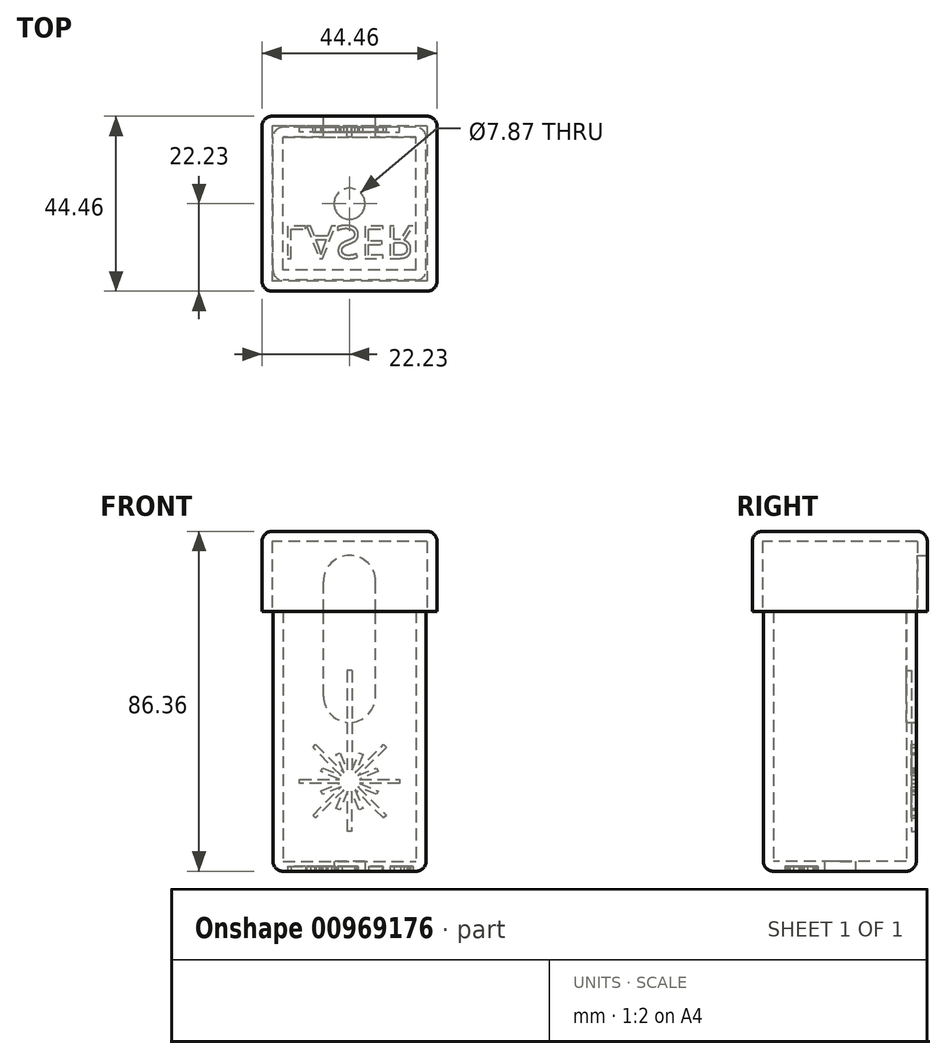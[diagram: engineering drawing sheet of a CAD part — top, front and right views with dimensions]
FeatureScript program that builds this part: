
annotation { "Feature Type Name" : "Feature", "Feature Type Description" : "" }
export const myFeature = defineFeature(function(context is Context, id is Id, definition is map)
    precondition{}
    {
        {
            var Q0;
            Q0=qCreatedBy(makeId("Top.planeOp"),FACE);
            var sketch = newSketch(context, id + "F0", { "sketchPlane" : qUnion([Q0])});
            skLineSegment(sketch, "E0.bottom", {"start": v(16.9, -16.9) * mm, "end": v(-16.9, -16.9) * mm});
            skLineSegment(sketch, "E0.top", {"start": v(16.9, 16.9) * mm, "end": v(-16.9, 16.9) * mm});
            skLineSegment(sketch, "E0.left", {"start": v(16.9, -16.9) * mm, "end": v(16.9, 16.9) * mm});
            skLineSegment(sketch, "E0.right", {"start": v(-16.9, -16.9) * mm, "end": v(-16.9, 16.9) * mm});
            skPoint(sketch, "E0.middle", {"position": v(0, 0) * mm});
            skLineSegment(sketch, "E1.bottom", {"start": v(19.43, -19.43) * mm, "end": v(-19.43, -19.43) * mm});
            skLineSegment(sketch, "E1.top", {"start": v(19.43, 19.43) * mm, "end": v(-19.43, 19.43) * mm});
            skLineSegment(sketch, "E1.left", {"start": v(19.43, -19.43) * mm, "end": v(19.43, 19.43) * mm});
            skLineSegment(sketch, "E1.right", {"start": v(-19.43, -19.43) * mm, "end": v(-19.43, 19.43) * mm});
            skSolve(sketch);
        }
        {
            var Q0;
            Q0=makeQuery(id+"F0.imprint","IMPRINT",FACE,{"disambiguationData":[TD([[makeQuery(id+"F0.imprint","IMPRINT",EDGE,{"derivedFrom":sQuery(id+"F0.wireOp",EDGE,"E0.bottom")}),1.0]])]});
            var Q1;
            Q1=makeQuery(id+"F0.imprint","IMPRINT",FACE,{"disambiguationData":[TD([[makeQuery(id+"F0.imprint","IMPRINT",EDGE,{"derivedFrom":sQuery(id+"F0.wireOp",EDGE,"E0.bottom")}),-1.0]])]});
            extrude(context, id + "F1", {"entities" : qUnion([Q0, Q1]), "depth" : 2.54 * mm, "offsetDistance" : 25.4 * mm});
        }
        {
            var Q0;
            Q0 = qSketchRegion(id + "F0", true);
            extrude(context, id + "F2", {"entities" : qUnion([Q0]), "operationType" : NewBodyOperationType.ADD, "depth" : 66.04 * mm, "offsetDistance" : 25.4 * mm});
        }
        {
            var Q0;
            {var subQ0=sQuery(id+"F0.wireOp",EDGE,"E1.left");var subQ1=sQuery(id+"F0.wireOp",EDGE,"E1.bottom");Q0=makeQuery(id+"F2.boolean.opBoolean","MERGE",EDGE,{"derivedFrom":[makeQuery(id+"F1.opExtrude","SWEPT_EDGE",EDGE,{"disambiguationData":[OSD([subQ1,subQ0])]}),makeQuery(id+"F2.opExtrude","SWEPT_EDGE",EDGE,{"disambiguationData":[OSD([subQ1,subQ0])]})]});}
            var Q1;
            {var subQ0=sQuery(id+"F0.wireOp",EDGE,"E1.left");var subQ1=sQuery(id+"F0.wireOp",EDGE,"E1.top");Q1=makeQuery(id+"F2.boolean.opBoolean","MERGE",EDGE,{"derivedFrom":[makeQuery(id+"F1.opExtrude","SWEPT_EDGE",EDGE,{"disambiguationData":[OSD([subQ1,subQ0])]}),makeQuery(id+"F2.opExtrude","SWEPT_EDGE",EDGE,{"disambiguationData":[OSD([subQ1,subQ0])]})]});}
            var Q2;
            Q2=makeQuery(id+"F1.opExtrude","CAP_EDGE",EDGE,{"disambiguationData":[OSD([sQuery(id+"F0.wireOp",EDGE,"E1.left")])],"isStart":true});
            var Q3;
            Q3=makeQuery(id+"F1.opExtrude","CAP_EDGE",EDGE,{"disambiguationData":[OSD([sQuery(id+"F0.wireOp",EDGE,"E1.bottom")])],"isStart":true});
            var Q4;
            {var subQ0=sQuery(id+"F0.wireOp",EDGE,"E1.right");var subQ1=sQuery(id+"F0.wireOp",EDGE,"E1.bottom");Q4=makeQuery(id+"F2.boolean.opBoolean","MERGE",EDGE,{"derivedFrom":[makeQuery(id+"F1.opExtrude","SWEPT_EDGE",EDGE,{"disambiguationData":[OSD([subQ1,subQ0])]}),makeQuery(id+"F2.opExtrude","SWEPT_EDGE",EDGE,{"disambiguationData":[OSD([subQ1,subQ0])]})]});}
            var Q5;
            Q5=makeQuery(id+"F1.opExtrude","CAP_EDGE",EDGE,{"disambiguationData":[OSD([sQuery(id+"F0.wireOp",EDGE,"E1.right")])],"isStart":true});
            var Q6;
            Q6=makeQuery(id+"F1.opExtrude","CAP_EDGE",EDGE,{"disambiguationData":[OSD([sQuery(id+"F0.wireOp",EDGE,"E1.top")])],"isStart":true});
            var Q7;
            {var subQ0=sQuery(id+"F0.wireOp",EDGE,"E1.right");var subQ1=sQuery(id+"F0.wireOp",EDGE,"E1.top");Q7=makeQuery(id+"F2.boolean.opBoolean","MERGE",EDGE,{"derivedFrom":[makeQuery(id+"F1.opExtrude","SWEPT_EDGE",EDGE,{"disambiguationData":[OSD([subQ1,subQ0])]}),makeQuery(id+"F2.opExtrude","SWEPT_EDGE",EDGE,{"disambiguationData":[OSD([subQ1,subQ0])]})]});}
            fillet(context, id + "F3", {"entities" : qUnion([Q0, Q1, Q2, Q3, Q4, Q5, Q6, Q7]), "radius" : 2.54 * mm, "tangentPropagation" : true, "allowEdgeOverflow" : false});
        }
        {
            var Q0;
            Q0=makeQuery(id+"F1.opExtrude","CAP_FACE",FACE,{"disambiguationData":[OSD([sQuery(id+"F0.wireOp",EDGE,"E1.bottom"),sQuery(id+"F0.wireOp",EDGE,"E1.top"),sQuery(id+"F0.wireOp",EDGE,"E1.left"),sQuery(id+"F0.wireOp",EDGE,"E1.right")])],"isStart":true});
            var sketch = newSketch(context, id + "F4", { "sketchPlane" : qUnion([Q0])});
            skCircle(sketch, "E2", {"center": v(0, 0) * mm, "radius": 3.94 * mm});
            skSolve(sketch);
        }
        {
            var Q0;
            Q0=makeQuery(id+"F4.imprint","IMPRINT",FACE,{"disambiguationData":[TD([[makeQuery(id+"F4.imprint","IMPRINT",EDGE,{"derivedFrom":sQuery(id+"F4.wireOp",EDGE,"E2")}),1.0]])]});
            extrude(context, id + "F5", {"entities" : qUnion([Q0]), "operationType" : NewBodyOperationType.REMOVE, "oppositeDirection" : true, "depth" : 25.4 * mm, "offsetDistance" : 25.4 * mm});
        }
        {
            var Q0;
            Q0=makeQuery(id+"F2.opExtrude","CAP_FACE",FACE,{"disambiguationData":[OSD([sQuery(id+"F0.wireOp",EDGE,"E0.bottom"),sQuery(id+"F0.wireOp",EDGE,"E0.top"),sQuery(id+"F0.wireOp",EDGE,"E0.left"),sQuery(id+"F0.wireOp",EDGE,"E0.right"),sQuery(id+"F0.wireOp",EDGE,"E1.bottom"),sQuery(id+"F0.wireOp",EDGE,"E1.top"),sQuery(id+"F0.wireOp",EDGE,"E1.left"),sQuery(id+"F0.wireOp",EDGE,"E1.right")])],"isStart":false});
            var sketch = newSketch(context, id + "F6", { "sketchPlane" : qUnion([Q0])});
            skLineSegment(sketch, "E3.bottom", {"start": v(19.69, 19.69) * mm, "end": v(-19.69, 19.69) * mm});
            skLineSegment(sketch, "E3.top", {"start": v(19.69, -19.69) * mm, "end": v(-19.69, -19.69) * mm});
            skLineSegment(sketch, "E3.left", {"start": v(19.69, 19.69) * mm, "end": v(19.69, -19.69) * mm});
            skLineSegment(sketch, "E3.right", {"start": v(-19.69, 19.69) * mm, "end": v(-19.69, -19.69) * mm});
            skPoint(sketch, "E3.middle", {"position": v(0, 0) * mm});
            skLineSegment(sketch, "E4.bottom", {"start": v(22.23, 22.23) * mm, "end": v(-22.23, 22.23) * mm});
            skLineSegment(sketch, "E4.top", {"start": v(22.23, -22.23) * mm, "end": v(-22.23, -22.23) * mm});
            skLineSegment(sketch, "E4.left", {"start": v(22.23, 22.23) * mm, "end": v(22.23, -22.23) * mm});
            skLineSegment(sketch, "E4.right", {"start": v(-22.23, 22.23) * mm, "end": v(-22.23, -22.23) * mm});
            skSolve(sketch);
        }
        {
            var Q0;
            Q0=makeQuery(id+"F6.imprint","IMPRINT",FACE,{"disambiguationData":[TD([[makeQuery(id+"F6.imprint","IMPRINT",EDGE,{"derivedFrom":sQuery(id+"F6.wireOp",EDGE,"E3.bottom")}),-1.0]])]});
            extrude(context, id + "F7", {"entities" : qUnion([Q0]), "depth" : 17.78 * mm, "offsetDistance" : 25.4 * mm});
        }
        {
            var Q0;
            Q0=makeQuery(id+"F7.opExtrude","CAP_FACE",FACE,{"disambiguationData":[OSD([sQuery(id+"F6.wireOp",EDGE,"E3.bottom"),sQuery(id+"F6.wireOp",EDGE,"E3.top"),sQuery(id+"F6.wireOp",EDGE,"E3.left"),sQuery(id+"F6.wireOp",EDGE,"E3.right"),sQuery(id+"F6.wireOp",EDGE,"E4.bottom"),sQuery(id+"F6.wireOp",EDGE,"E4.top"),sQuery(id+"F6.wireOp",EDGE,"E4.left"),sQuery(id+"F6.wireOp",EDGE,"E4.right")])],"isStart":false});
            var sketch = newSketch(context, id + "F8", { "sketchPlane" : qUnion([Q0])});
            skLineSegment(sketch, "E5.bottom", {"start": v(19.69, 19.69) * mm, "end": v(-19.69, 19.69) * mm});
            skLineSegment(sketch, "E5.top", {"start": v(19.69, -19.69) * mm, "end": v(-19.69, -19.69) * mm});
            skLineSegment(sketch, "E5.left", {"start": v(19.69, 19.69) * mm, "end": v(19.69, -19.69) * mm});
            skLineSegment(sketch, "E5.right", {"start": v(-19.69, 19.69) * mm, "end": v(-19.69, -19.69) * mm});
            skPoint(sketch, "E5.middle", {"position": v(0, 0) * mm});
            skLineSegment(sketch, "E6.bottom", {"start": v(22.22, 22.23) * mm, "end": v(-22.23, 22.23) * mm});
            skLineSegment(sketch, "E6.top", {"start": v(22.22, -22.23) * mm, "end": v(-22.23, -22.23) * mm});
            skLineSegment(sketch, "E6.left", {"start": v(22.22, 22.23) * mm, "end": v(22.22, -22.23) * mm});
            skLineSegment(sketch, "E6.right", {"start": v(-22.23, 22.23) * mm, "end": v(-22.23, -22.23) * mm});
            skSolve(sketch);
        }
        {
            var Q0;
            Q0=makeQuery(id+"F8.imprint","IMPRINT",FACE,{"disambiguationData":[TD([[makeQuery(id+"F8.imprint","IMPRINT",EDGE,{"derivedFrom":sQuery(id+"F8.wireOp",EDGE,"E5.bottom")}),1.0]])]});
            var Q1;
            Q1=makeQuery(id+"F8.imprint","IMPRINT",FACE,{"disambiguationData":[TD([[makeQuery(id+"F8.imprint","IMPRINT",EDGE,{"derivedFrom":sQuery(id+"F8.wireOp",EDGE,"E5.bottom")}),-1.0]])]});
            extrude(context, id + "F9", {"entities" : qUnion([Q0, Q1]), "operationType" : NewBodyOperationType.ADD, "depth" : 2.54 * mm, "offsetDistance" : 25.4 * mm});
        }
        {
            var Q0;
            Q0=makeQuery(id+"F9.boolean.opBoolean","MERGE",EDGE,{"derivedFrom":[makeQuery(id+"F7.opExtrude","SWEPT_EDGE",EDGE,{"disambiguationData":[OSD([sQuery(id+"F6.wireOp",EDGE,"E4.top"),sQuery(id+"F6.wireOp",EDGE,"E4.left")])]}),makeQuery(id+"F9.opExtrude","SWEPT_EDGE",EDGE,{"disambiguationData":[OSD([sQuery(id+"F8.wireOp",EDGE,"E6.top"),sQuery(id+"F8.wireOp",EDGE,"E6.left")])]})]});
            var Q1;
            Q1=makeQuery(id+"F9.opExtrude","CAP_EDGE",EDGE,{"disambiguationData":[OSD([sQuery(id+"F8.wireOp",EDGE,"E6.left")])],"isStart":false});
            var Q2;
            Q2=makeQuery(id+"F9.opExtrude","CAP_EDGE",EDGE,{"disambiguationData":[OSD([sQuery(id+"F8.wireOp",EDGE,"E6.top")])],"isStart":false});
            var Q3;
            Q3=makeQuery(id+"F9.boolean.opBoolean","MERGE",EDGE,{"derivedFrom":[makeQuery(id+"F7.opExtrude","SWEPT_EDGE",EDGE,{"disambiguationData":[OSD([sQuery(id+"F6.wireOp",EDGE,"E4.bottom"),sQuery(id+"F6.wireOp",EDGE,"E4.left")])]}),makeQuery(id+"F9.opExtrude","SWEPT_EDGE",EDGE,{"disambiguationData":[OSD([sQuery(id+"F8.wireOp",EDGE,"E6.bottom"),sQuery(id+"F8.wireOp",EDGE,"E6.left")])]})]});
            var Q4;
            Q4=makeQuery(id+"F9.opExtrude","CAP_EDGE",EDGE,{"disambiguationData":[OSD([sQuery(id+"F8.wireOp",EDGE,"E6.bottom")])],"isStart":false});
            var Q5;
            Q5=makeQuery(id+"F9.boolean.opBoolean","MERGE",EDGE,{"derivedFrom":[makeQuery(id+"F7.opExtrude","SWEPT_EDGE",EDGE,{"disambiguationData":[OSD([sQuery(id+"F6.wireOp",EDGE,"E4.bottom"),sQuery(id+"F6.wireOp",EDGE,"E4.right")])]}),makeQuery(id+"F9.opExtrude","SWEPT_EDGE",EDGE,{"disambiguationData":[OSD([sQuery(id+"F8.wireOp",EDGE,"E6.bottom"),sQuery(id+"F8.wireOp",EDGE,"E6.right")])]})]});
            var Q6;
            Q6=makeQuery(id+"F9.opExtrude","CAP_EDGE",EDGE,{"disambiguationData":[OSD([sQuery(id+"F8.wireOp",EDGE,"E6.right")])],"isStart":false});
            var Q7;
            Q7=makeQuery(id+"F9.boolean.opBoolean","MERGE",EDGE,{"derivedFrom":[makeQuery(id+"F7.opExtrude","SWEPT_EDGE",EDGE,{"disambiguationData":[OSD([sQuery(id+"F6.wireOp",EDGE,"E4.top"),sQuery(id+"F6.wireOp",EDGE,"E4.right")])]}),makeQuery(id+"F9.opExtrude","SWEPT_EDGE",EDGE,{"disambiguationData":[OSD([sQuery(id+"F8.wireOp",EDGE,"E6.top"),sQuery(id+"F8.wireOp",EDGE,"E6.right")])]})]});
            fillet(context, id + "F10", {"entities" : qUnion([Q0, Q1, Q2, Q3, Q4, Q5, Q6, Q7]), "radius" : 2.54 * mm, "tangentPropagation" : true, "allowEdgeOverflow" : false});
        }
        {
            var Q0;
            {var subQ0=sQuery(id+"F0.wireOp",EDGE,"E1.top");Q0=makeQuery(id+"F2.boolean.opBoolean","MERGE",FACE,{"derivedFrom":[makeQuery(id+"F1.opExtrude","SWEPT_FACE",FACE,{"disambiguationData":[OSD([subQ0])]}),makeQuery(id+"F2.opExtrude","SWEPT_FACE",FACE,{"disambiguationData":[OSD([subQ0])]})]});}
            var sketch = newSketch(context, id + "F11", { "sketchPlane" : qUnion([Q0])});
            skCircle(sketch, "E7.cCircle", {"center": v(0, 22.86) * mm, "radius": 2.54 * mm, "construction": true});
            skLineSegment(sketch, "E7.0", {"start": v(2.54, 23.37) * mm, "end": v(2.54, 22.35) * mm});
            skLineSegment(sketch, "E7.1", {"start": v(2.54, 22.35) * mm, "end": v(2.15, 21.42) * mm});
            skLineSegment(sketch, "E7.2", {"start": v(2.15, 21.42) * mm, "end": v(1.44, 20.7) * mm});
            skLineSegment(sketch, "E7.3", {"start": v(1.44, 20.7) * mm, "end": v(0.5, 20.32) * mm});
            skLineSegment(sketch, "E7.4", {"start": v(0.5, 20.32) * mm, "end": v(-0.5, 20.32) * mm});
            skLineSegment(sketch, "E7.5", {"start": v(-0.5, 20.32) * mm, "end": v(-1.44, 20.7) * mm});
            skLineSegment(sketch, "E7.6", {"start": v(-1.44, 20.7) * mm, "end": v(-2.15, 21.42) * mm});
            skLineSegment(sketch, "E7.7", {"start": v(-2.15, 21.42) * mm, "end": v(-2.54, 22.35) * mm});
            skLineSegment(sketch, "E7.8", {"start": v(-2.54, 22.35) * mm, "end": v(-2.54, 23.37) * mm});
            skLineSegment(sketch, "E7.9", {"start": v(-2.54, 23.37) * mm, "end": v(-2.15, 24.3) * mm});
            skLineSegment(sketch, "E7.10", {"start": v(-2.15, 24.3) * mm, "end": v(-1.44, 25.01) * mm});
            skLineSegment(sketch, "E7.11", {"start": v(-1.44, 25.01) * mm, "end": v(-0.5, 25.4) * mm});
            skLineSegment(sketch, "E7.12", {"start": v(-0.5, 25.4) * mm, "end": v(0.5, 25.4) * mm});
            skLineSegment(sketch, "E7.13", {"start": v(0.5, 25.4) * mm, "end": v(1.44, 25.01) * mm});
            skLineSegment(sketch, "E7.14", {"start": v(1.44, 25.01) * mm, "end": v(2.15, 24.3) * mm});
            skLineSegment(sketch, "E7.15", {"start": v(2.15, 24.3) * mm, "end": v(2.54, 23.37) * mm});
            skPoint(sketch, "E7.0.midPoint", {"position": v(2.54, 22.86) * mm});
            skLineSegment(sketch, "E8", {"start": v(-1.44, 25.01) * mm, "end": v(-8.62, 32.2) * mm});
            skLineSegment(sketch, "E9", {"start": v(-8.62, 32.2) * mm, "end": v(-9.34, 31.48) * mm});
            skLineSegment(sketch, "E10", {"start": v(-9.34, 31.48) * mm, "end": v(-2.15, 24.3) * mm});
            skLineSegment(sketch, "E11.anchor1", {"start": v(0, 22.86) * mm, "end": v(-2.15, 24.3) * mm, "construction": true});
            skLineSegment(sketch, "E11.anchor2", {"start": v(0, 22.86) * mm, "end": v(-2.15, 24.3) * mm, "construction": true});
            skLineSegment(sketch, "E12.1.0", {"start": v(-2.54, 23.37) * mm, "end": v(-12.7, 23.37) * mm});
            skLineSegment(sketch, "E12.1.1", {"start": v(-12.7, 22.35) * mm, "end": v(-2.54, 22.35) * mm});
            skLineSegment(sketch, "E12.1.2", {"start": v(-12.7, 23.37) * mm, "end": v(-12.7, 22.35) * mm});
            skLineSegment(sketch, "E12.2.0", {"start": v(-2.15, 21.42) * mm, "end": v(-9.34, 14.24) * mm});
            skLineSegment(sketch, "E12.2.1", {"start": v(-8.62, 13.52) * mm, "end": v(-1.44, 20.7) * mm});
            skLineSegment(sketch, "E12.2.2", {"start": v(-9.34, 14.24) * mm, "end": v(-8.62, 13.52) * mm});
            skLineSegment(sketch, "E12.3.0", {"start": v(-0.5, 20.32) * mm, "end": v(-0.5, 10.16) * mm});
            skLineSegment(sketch, "E12.3.1", {"start": v(0.5, 10.16) * mm, "end": v(0.5, 20.32) * mm});
            skLineSegment(sketch, "E12.3.2", {"start": v(-0.5, 10.16) * mm, "end": v(0.5, 10.16) * mm});
            skLineSegment(sketch, "E12.4.0", {"start": v(1.44, 20.7) * mm, "end": v(8.62, 13.52) * mm});
            skLineSegment(sketch, "E12.4.1", {"start": v(9.34, 14.24) * mm, "end": v(2.15, 21.42) * mm});
            skLineSegment(sketch, "E12.4.2", {"start": v(8.62, 13.52) * mm, "end": v(9.34, 14.24) * mm});
            skLineSegment(sketch, "E12.5.0", {"start": v(2.54, 22.35) * mm, "end": v(12.7, 22.35) * mm});
            skLineSegment(sketch, "E12.5.1", {"start": v(12.7, 23.37) * mm, "end": v(2.54, 23.37) * mm});
            skLineSegment(sketch, "E12.5.2", {"start": v(12.7, 22.35) * mm, "end": v(12.7, 23.37) * mm});
            skLineSegment(sketch, "E12.6.0", {"start": v(2.15, 24.3) * mm, "end": v(9.34, 31.48) * mm});
            skLineSegment(sketch, "E12.6.1", {"start": v(8.62, 32.2) * mm, "end": v(1.44, 25.01) * mm});
            skLineSegment(sketch, "E12.6.2", {"start": v(9.34, 31.48) * mm, "end": v(8.62, 32.2) * mm});
            skLineSegment(sketch, "E12.7.0", {"start": v(0.5, 25.4) * mm, "end": v(0.5, 35.56) * mm});
            skLineSegment(sketch, "E12.7.1", {"start": v(-0.5, 35.56) * mm, "end": v(-0.5, 25.4) * mm});
            skLineSegment(sketch, "E12.7.2", {"start": v(0.5, 35.56) * mm, "end": v(-0.5, 35.56) * mm});
            skLineSegment(sketch, "E13", {"start": v(-2.15, 24.3) * mm, "end": v(-6.85, 26.24) * mm});
            skLineSegment(sketch, "E14", {"start": v(-6.85, 26.24) * mm, "end": v(-7.23, 25.3) * mm});
            skLineSegment(sketch, "E15", {"start": v(-7.23, 25.3) * mm, "end": v(-2.54, 23.37) * mm});
            skLineSegment(sketch, "E16.1.0", {"start": v(-2.54, 22.35) * mm, "end": v(-7.23, 20.41) * mm});
            skLineSegment(sketch, "E16.1.1", {"start": v(-7.23, 20.41) * mm, "end": v(-6.85, 19.48) * mm});
            skLineSegment(sketch, "E16.1.2", {"start": v(-6.85, 19.48) * mm, "end": v(-2.15, 21.42) * mm});
            skLineSegment(sketch, "E16.2.0", {"start": v(-1.44, 20.7) * mm, "end": v(-3.38, 16.01) * mm});
            skLineSegment(sketch, "E16.2.1", {"start": v(-3.38, 16.01) * mm, "end": v(-2.45, 15.63) * mm});
            skLineSegment(sketch, "E16.2.2", {"start": v(-2.45, 15.63) * mm, "end": v(-0.5, 20.32) * mm});
            skLineSegment(sketch, "E16.3.0", {"start": v(0.5, 20.32) * mm, "end": v(2.45, 15.63) * mm});
            skLineSegment(sketch, "E16.3.1", {"start": v(2.45, 15.63) * mm, "end": v(3.38, 16.01) * mm});
            skLineSegment(sketch, "E16.3.2", {"start": v(3.38, 16.01) * mm, "end": v(1.44, 20.7) * mm});
            skLineSegment(sketch, "E16.4.0", {"start": v(2.15, 21.42) * mm, "end": v(6.85, 19.48) * mm});
            skLineSegment(sketch, "E16.4.1", {"start": v(6.85, 19.48) * mm, "end": v(7.23, 20.41) * mm});
            skLineSegment(sketch, "E16.4.2", {"start": v(7.23, 20.41) * mm, "end": v(2.54, 22.35) * mm});
            skLineSegment(sketch, "E16.5.0", {"start": v(2.54, 23.37) * mm, "end": v(7.23, 25.3) * mm});
            skLineSegment(sketch, "E16.5.1", {"start": v(7.23, 25.3) * mm, "end": v(6.85, 26.24) * mm});
            skLineSegment(sketch, "E16.5.2", {"start": v(6.85, 26.24) * mm, "end": v(2.15, 24.3) * mm});
            skLineSegment(sketch, "E16.6.0", {"start": v(1.44, 25.01) * mm, "end": v(3.38, 29.7) * mm});
            skLineSegment(sketch, "E16.6.1", {"start": v(3.38, 29.7) * mm, "end": v(2.45, 30.1) * mm});
            skLineSegment(sketch, "E16.6.2", {"start": v(2.45, 30.1) * mm, "end": v(0.5, 25.4) * mm});
            skLineSegment(sketch, "E16.7.0", {"start": v(-0.5, 25.4) * mm, "end": v(-2.45, 30.1) * mm});
            skLineSegment(sketch, "E16.7.1", {"start": v(-2.45, 30.1) * mm, "end": v(-3.38, 29.7) * mm});
            skLineSegment(sketch, "E16.7.2", {"start": v(-3.38, 29.7) * mm, "end": v(-1.44, 25.01) * mm});
            skLineSegment(sketch, "E17", {"start": v(0, 66.04) * mm, "end": v(0, 44.45) * mm});
            skLineSegment(sketch, "E18", {"start": v(0, 44.45) * mm, "end": v(0, 22.86) * mm});
            skLineSegment(sketch, "E19.bottom", {"start": v(0.62, 66.04) * mm, "end": v(-0.62, 66.04) * mm});
            skLineSegment(sketch, "E19.top", {"start": v(0.62, 22.86) * mm, "end": v(-0.62, 22.86) * mm});
            skLineSegment(sketch, "E19.left", {"start": v(0.62, 66.04) * mm, "end": v(0.62, 22.86) * mm});
            skLineSegment(sketch, "E19.right", {"start": v(-0.62, 66.04) * mm, "end": v(-0.62, 22.86) * mm});
            skPoint(sketch, "E19.middle", {"position": v(0, 44.45) * mm});
            skSolve(sketch);
        }
        {
            var Q0;
            Q0=makeQuery(id+"F1.opExtrude","CAP_FACE",FACE,{"disambiguationData":[OSD([sQuery(id+"F0.wireOp",EDGE,"E1.bottom"),sQuery(id+"F0.wireOp",EDGE,"E1.top"),sQuery(id+"F0.wireOp",EDGE,"E1.left"),sQuery(id+"F0.wireOp",EDGE,"E1.right")])],"isStart":true});
            var sketch = newSketch(context, id + "F12", { "sketchPlane" : qUnion([Q0])});
            skText(sketch, "E20", { "text": "LASER\n", "fontName": "OpenSans-Regular.ttf"});
            const initialGuessF12  = {"E20": [-0.0169, 0.00562, 1, 0, 0.00832]};
            skSetInitialGuess(sketch, initialGuessF12);
            skSolve(sketch);
        }
        {
            var Q0;
            Q0 = qSketchRegion(id + "F12", true);
            extrude(context, id + "F13", {"entities" : qUnion([Q0]), "operationType" : NewBodyOperationType.REMOVE, "oppositeDirection" : true, "depth" : 1.27 * mm, "offsetDistance" : 25.4 * mm});
        }
        {
            var Q0;
            Q0 = qSketchRegion(id + "F11", true);
            var Q1;
            {var subQ0=sQuery(id+"F11.wireOp",EDGE,"E19.top");var subQ1=sQuery(id+"F11.wireOp",EDGE,"E18");var subQ2=makeQuery(id+"F11.imprint","INTERSECT",VERTEX,{"derivedFrom":[subQ1,subQ0]});Q1=makeQuery(id+"F11.imprint","IMPRINT",FACE,{"disambiguationData":[TD([[makeQuery(id+"F11.imprint","IMPRINT",EDGE,{"disambiguationData":[TD([[subQ2,1.0]])],"derivedFrom":subQ1}),1.0]])]});}
            var Q2;
            {var subQ0=sQuery(id+"F11.wireOp",EDGE,"E12.7.1");Q2=makeQuery(id+"F11.imprint","IMPRINT",FACE,{"disambiguationData":[TD([[makeQuery(id+"F11.imprint","IMPRINT",EDGE,{"derivedFrom":subQ0}),1.0]])]});}
            var Q3;
            {var subQ0=sQuery(id+"F11.wireOp",EDGE,"E19.top");var subQ1=sQuery(id+"F11.wireOp",EDGE,"E18");var subQ2=makeQuery(id+"F11.imprint","INTERSECT",VERTEX,{"derivedFrom":[subQ1,subQ0]});Q3=makeQuery(id+"F11.imprint","IMPRINT",FACE,{"disambiguationData":[TD([[makeQuery(id+"F11.imprint","IMPRINT",EDGE,{"disambiguationData":[TD([[subQ2,1.0]])],"derivedFrom":subQ1}),-1.0]])]});}
            var Q4;
            {var subQ0=sQuery(id+"F11.wireOp",EDGE,"E12.7.0");Q4=makeQuery(id+"F11.imprint","IMPRINT",FACE,{"disambiguationData":[TD([[makeQuery(id+"F11.imprint","IMPRINT",EDGE,{"derivedFrom":subQ0}),1.0]])]});}
            extrude(context, id + "F14", {"entities" : qUnion([Q0, Q1, Q2, Q3, Q4]), "operationType" : NewBodyOperationType.REMOVE, "oppositeDirection" : true, "depth" : 1.27 * mm, "offsetDistance" : 25.4 * mm});
        }
        {
            var Q0;
            Q0=qCreatedBy(makeId("Right.planeOp"),FACE);
            var sketch = newSketch(context, id + "F15", { "sketchPlane" : qUnion([Q0])});
            skLineSegment(sketch, "E21", {"start": v(0, -76.45) * mm, "end": v(0, 0) * mm});
            skSolve(sketch);
        }
        {
            var Q0;
            {var subQ0=sQuery(id+"F0.wireOp",EDGE,"E1.top");Q0=makeQuery(id+"F2.boolean.opBoolean","MERGE",FACE,{"derivedFrom":[makeQuery(id+"F1.opExtrude","SWEPT_FACE",FACE,{"disambiguationData":[OSD([subQ0])]}),makeQuery(id+"F2.opExtrude","SWEPT_FACE",FACE,{"disambiguationData":[OSD([subQ0])]})]});}
            var sketch = newSketch(context, id + "F16", { "sketchPlane" : qUnion([Q0])});
            skCircle(sketch, "E22", {"center": v(0, 73.66) * mm, "radius": 6.6 * mm});
            skLineSegment(sketch, "E23", {"start": v(-6.6, 73.66) * mm, "end": v(-6.6, 44.45) * mm});
            skLineSegment(sketch, "E24", {"start": v(6.6, 73.66) * mm, "end": v(6.6, 44.45) * mm});
            skCircle(sketch, "E25", {"center": v(0, 44.45) * mm, "radius": 6.6 * mm});
            skSolve(sketch);
        }
        {
            var Q0;
            {var subQ0=sQuery(id+"F16.wireOp",EDGE,"E22");var subQ1=makeQuery(id+"F16.imprint","INTERSECT",VERTEX,{"derivedFrom":[subQ0,sQuery(id+"F16.wireOp",EDGE,"E23")]});Q0=makeQuery(id+"F16.imprint","IMPRINT",FACE,{"disambiguationData":[TD([[makeQuery(id+"F16.imprint","IMPRINT",EDGE,{"disambiguationData":[TD([[subQ1,1.0]])],"derivedFrom":subQ0}),1.0]])]});}
            var Q1;
            {var subQ0=sQuery(id+"F16.wireOp",EDGE,"E23");var subQ1=sQuery(id+"F16.wireOp",EDGE,"E22");var subQ2=makeQuery(id+"F16.imprint","INTERSECT",VERTEX,{"derivedFrom":[subQ1,subQ0]});Q1=makeQuery(id+"F16.imprint","IMPRINT",FACE,{"disambiguationData":[TD([[makeQuery(id+"F16.imprint","IMPRINT",EDGE,{"disambiguationData":[TD([[subQ2,-1.0]])],"derivedFrom":subQ1}),-1.0]])]});}
            var Q2;
            {var subQ0=sQuery(id+"F16.wireOp",EDGE,"E25");var subQ1=sQuery(id+"F16.wireOp",EDGE,"E23");var subQ2=makeQuery(id+"F16.imprint","INTERSECT",VERTEX,{"derivedFrom":[subQ1,subQ0]});Q2=makeQuery(id+"F16.imprint","IMPRINT",FACE,{"disambiguationData":[TD([[makeQuery(id+"F16.imprint","IMPRINT",EDGE,{"disambiguationData":[TD([[subQ2,1.0]])],"derivedFrom":subQ1}),1.0]])]});}
            var Q3;
            {var subQ0=sQuery(id+"F16.wireOp",EDGE,"E25");var subQ1=makeQuery(id+"F16.imprint","INTERSECT",VERTEX,{"derivedFrom":[sQuery(id+"F16.wireOp",EDGE,"E23"),subQ0]});Q3=makeQuery(id+"F16.imprint","IMPRINT",FACE,{"disambiguationData":[TD([[makeQuery(id+"F16.imprint","IMPRINT",EDGE,{"disambiguationData":[TD([[subQ1,1.0]])],"derivedFrom":subQ0}),1.0]])]});}
            var Q4;
            {var subQ0=sQuery(id+"F16.wireOp",EDGE,"E25");var subQ1=sQuery(id+"F16.wireOp",EDGE,"E24");var subQ2=makeQuery(id+"F16.imprint","INTERSECT",VERTEX,{"derivedFrom":[subQ1,subQ0]});Q4=makeQuery(id+"F16.imprint","IMPRINT",FACE,{"disambiguationData":[TD([[makeQuery(id+"F16.imprint","IMPRINT",EDGE,{"disambiguationData":[TD([[subQ2,-1.0]])],"derivedFrom":subQ0}),-1.0]])]});}
            var Q5;
            {var subQ0=sQuery(id+"F16.wireOp",EDGE,"E25");var subQ1=makeQuery(id+"F16.imprint","INTERSECT",VERTEX,{"derivedFrom":[sQuery(id+"F16.wireOp",EDGE,"E24"),subQ0]});Q5=makeQuery(id+"F16.imprint","IMPRINT",FACE,{"disambiguationData":[TD([[makeQuery(id+"F16.imprint","IMPRINT",EDGE,{"disambiguationData":[TD([[subQ1,-1.0]])],"derivedFrom":subQ0}),1.0]])]});}
            var Q6;
            {var subQ0=sQuery(id+"F16.wireOp",EDGE,"E25");var subQ1=makeQuery(id+"F14.boolean.opBoolean","COPY",EDGE,{"derivedFrom":makeQuery(id+"F14.opExtrude","CAP_EDGE",EDGE,{"disambiguationData":[OSD([sQuery(id+"F11.wireOp",EDGE,"E19.left")])],"isStart":true})});var subQ2=makeQuery(id+"F16.imprint","INTERSECT",VERTEX,{"disambiguationData":[OD(0.0)],"derivedFrom":[subQ1,subQ0]});Q6=makeQuery(id+"F16.imprint","IMPRINT",FACE,{"disambiguationData":[TD([[makeQuery(id+"F16.imprint","IMPRINT",EDGE,{"disambiguationData":[TD([[subQ2,-1.0]])],"derivedFrom":subQ0}),1.0]])]});}
            extrude(context, id + "F17", {"entities" : qUnion([Q0, Q1, Q2, Q3, Q4, Q5, Q6]), "operationType" : NewBodyOperationType.REMOVE, "endBound" : BoundingType.SYMMETRIC, "oppositeDirection" : true, "depth" : 25.4 * mm, "offsetDistance" : 25.4 * mm});
        }
    });
